# Revit family: MECON mag-flux T4_remote flange
name_source: partatom
category: Rohrzubehör
units: mm (PartAtom-declared; Revit-internal decimal feet)

## family parameters
Arbeitsebenenbasiert = Nein
Beim Laden mit Abzugskörper schneiden = Nein
Bemaßung runder Anschluss = Radius verwenden
Gemeinsam genutzt = Nein
Immer vertikal = Ja
OmniClass-Nummer = 23.60.10.17
OmniClass-Titel = Flow Meters
Teiletyp = Ventil - Zerlegung in

## types (14) — shared parameters
Approval = VdS
Black = Metal - black
Dark Grey = Metal - RAL7024
Delivery Time = app. 3 weeks
Download Test Certificate = https://download.mecon.de
Glass = Glass-
Grey = Metal - grey
Hersteller = MECON GmbH, Röntgenstraße 105, 50169 Kerpen, Germany
IfcExportAs = IfcFlowMeter
IfcExportType = FLOWMETER
Operating Manual = https://www.mecon.de
URL = https://www.mecon.de
VdS Approval = https://www.mecon.de
Website Product = https://www.mecon.de
iFM = Nein
iLPCB = Nein
iVdS = Ja
zero-valued in all types: Vorgabe-Ansicht

## per-type parameters (varying)
| type | Build in Length | Flow Range | Modell | Nominal_Diameter | Nominal_Radius | Order Code | iB | iD1 | iD2 | iH | iR1 |
| DN 300 / PN 16, 0-42411 l/min, 0-11200 USgpm | 500 mm | 0 - 42411 l/min / 0 - 11200 USgpm | Flange connection DN 300 PN 16, lining: hard rubber, electrodes: stainless steel, remote, 230 V AC, 50/60 Hz, 4 - 20 mA, with connector for transducer | 300 mm | 150 mm | T4-H-D300-1-21BB4L | 200 mm  [stored 0.656168 ft] | 520 mm | 310 mm | 213 mm  [stored 0.698819 ft] | 154 mm  [stored 0.505249 ft] |
| DN 250 / PN 16, 0-29500 l/min, 0-7800 USgpm | 450 mm | 0 - 29500 l/min / 0 - 7800 USgpm | Flange connection DN 250 PN 16, lining: hard rubber, electrodes: stainless steel, remote, 230 V AC, 50/60 Hz, 4 - 20 mA, with connector for transducer | 250 mm | 125 mm | T4-H-D250-1-21BB4L | 200 mm  [stored 0.656168 ft] | 440 mm | 270 mm | 180 mm  [stored 0.590551 ft] | 129 mm  [stored 0.423228 ft] |
| DN 200 / PN 16, 0-18850 l/min, 0-5000 USgpm | 350 mm | 0 - 18850 l/min / 0 - 5000 USgpm | Flange connection DN 200 PN 16, lining: hard rubber, electrodes: stainless steel, remote, 230 V AC, 50/60 Hz, 4 - 20 mA, with connector for transducer | 200 mm | 100 mm | T4-H-D200-1-21BB4L | 200 mm  [stored 0.656168 ft] | 350 mm | 225 mm  [stored 0.738189 ft] | 143 mm | 104 mm |
| DN 150 / PN 16, 0-10600 l/min, 0-2800 USgpm | 300 mm | 0 - 10600 l/min / 0 - 2800 USgpm | Flange connection DN 150 PN 16, lining: hard rubber, electrodes: stainless steel, remote, 230 V AC, 50/60 Hz, 4 - 20 mA, with connector for transducer | 150 mm | 75 mm | T4-H-D150-1-21BB4L | 120 mm  [stored 0.393701 ft] | 285 mm | 192.5 mm  [stored 0.631562 ft] | 117 mm  [stored 0.383858 ft] | 79 mm |
| DN 125 / PN 16, 0-7350 l/min, 0-1950 USgpm | 250 mm | 0 - 7350 l/min / 0 - 1950 USgpm | Flange connection DN 125 PN 16, lining: hard rubber, electrodes: stainless steel, remote, 230 V AC, 50/60 Hz, 4 - 20 mA, with connector for transducer | 125 mm | 63 mm | T4-H-D125-1-21BB4L | 120 mm  [stored 0.393701 ft] | 240 mm  [stored 0.787402 ft] | 170 mm  [stored 0.557743 ft] | 98 mm  [stored 0.321522 ft] | 66.5 mm |
| DN 100 / PN 16, 0-4700 l/min, 0-1250 USgpm | 250 mm | 0 - 4700 l/min / 0 - 1250 USgpm | Flange connection DN 100 PN 16, lining: hard rubber, electrodes: stainless steel, remote, 230 V AC, 50/60 Hz, 4 - 20 mA, with connector for transducer | 100 mm | 50 mm | T4-H-D100-1-21BB4L | 120 mm  [stored 0.393701 ft] | 210 mm  [stored 0.688976 ft] | 155 mm  [stored 0.50853 ft] | 86 mm  [stored 0.282152 ft] | 54 mm |
| DN 80 / PN 16, 0-3000 l/min, 0-800 USgpm | 200 mm  [stored 0.656168 ft] | 0 - 3000 l/min / 0 - 800 USgpm | Flange connection DN 80 PN 16, lining: hard rubber, electrodes: stainless steel, remote, 230 V AC, 50/60 Hz, 4 - 20 mA, with connector for transducer | 80 mm | 40 mm | T4-H-D080-1-21BB4L | 80 mm  [stored 0.262467 ft] | 170 mm  [stored 0.557743 ft] | 135 mm  [stored 0.442913 ft] | 70 mm  [stored 0.229659 ft] | 44 mm  [stored 0.144357 ft] |
| DN 65 / PN 16, 0-2000 l/min, 0-525 USgpm | 200 mm  [stored 0.656168 ft] | 0 - 2000 l/min / 0 - 525 USgpm | Flange connection DN 65 PN 16, lining: hard rubber, electrodes: stainless steel, remote, 230 V AC, 50/60 Hz, 4 - 20 mA, with connector for transducer | 65 mm | 33 mm | T4-H-D065-1-21BB4L | 80 mm  [stored 0.262467 ft] | 155 mm  [stored 0.50853 ft] | 127.5 mm  [stored 0.418307 ft] | 63 mm  [stored 0.206693 ft] | 36.5 mm  [stored 0.119751 ft] |
| DN 50 / PN 40, 0-1180 l/min, 0-310 USgpm | 200 mm  [stored 0.656168 ft] | 0 - 1180 l/min / 0 - 310 USgpm | Flange connection DN 50 PN 40, lining: hard rubber, electrodes: stainless steel, remote, 230 V AC, 50/60 Hz, 4 - 20 mA, with connector for transducer | 50 mm | 25 mm | T4-H-D050-1-21BB4L | 80 mm  [stored 0.262467 ft] | 140 mm  [stored 0.459318 ft] | 120 mm  [stored 0.393701 ft] | 57 mm  [stored 0.187008 ft] | 29 mm  [stored 0.0951444 ft] |
| DN 40 / PN 40, 0-750 l/min, 0-200 USgpm | 200 mm  [stored 0.656168 ft] | 0 - 750 l/min / 0 - 200 USgpm | Flange connection DN 40 PN 40, lining: hard rubber, electrodes: stainless steel, remote, 230 V AC, 50/60 Hz, 4 - 20 mA, with connector for transducer | 40 mm | 20 mm | T4-H-D040-1-21BB4L | 80 mm  [stored 0.262467 ft] | 130 mm  [stored 0.426509 ft] | 115 mm  [stored 0.377297 ft] | 53 mm  [stored 0.173885 ft] | 24 mm  [stored 0.0787402 ft] |
| DN 32 / PN 40, 0-480 l/min, 0-128 USgpm | 200 mm  [stored 0.656168 ft] | 0 - 480 l/min / 0 - 128 USgpm | Flange connection DN 32 PN 40, lining: hard rubber, electrodes: stainless steel, remote, 230 V AC, 50/60 Hz, 4 - 20 mA, with connector for transducer | 32 mm | 16 mm | T4-H-D032-1-21BB4L | 80 mm  [stored 0.262467 ft] | 130 mm  [stored 0.426509 ft] | 115 mm  [stored 0.377297 ft] | 53 mm  [stored 0.173885 ft] | 20 mm  [stored 0.0656168 ft] |
| DN 25 / PN 40, 0-295 l/min, 0-78 USgpm | 200 mm  [stored 0.656168 ft] | 0 - 295 l/min / 0 - 78 USgpm | Flange connection DN 25 PN 40, lining: hard rubber, electrodes: stainless steel, remote, 230 V AC, 50/60 Hz, 4 - 20 mA, with connector for transducer | 25 mm | 13 mm | T4-H-D025-1-21BB4L | 80 mm  [stored 0.262467 ft] | 130 mm  [stored 0.426509 ft] | 115 mm  [stored 0.377297 ft] | 53 mm  [stored 0.173885 ft] | 16.5 mm  [stored 0.0541339 ft] |
| DN 20 / PN 40, 0-188 l/min, 0-50 USgpm | 200 mm  [stored 0.656168 ft] | 0 - 188 l/min / 0 - 50 USgpm | Flange connection DN 20 PN 40, lining: hard rubber, electrodes: stainless steel, remote, 230 V AC, 50/60 Hz, 4 - 20 mA, with connector for transducer | 20 mm | 10 mm | T4-H-D020-1-21BB4L | 80 mm  [stored 0.262467 ft] | 130 mm  [stored 0.426509 ft] | 115 mm  [stored 0.377297 ft] | 53 mm  [stored 0.173885 ft] | 14 mm  [stored 0.0459318 ft] |
| DN 15 / PN 40, 0-106 l/min, 0-28 USgpm | 200 mm  [stored 0.656168 ft] | 0 - 106 l/min / 0 - 28 USgpm | Flange connection: DN 15 PN 40, lining: hard rubber, electrodes: stainless steel, remote, 230 V AC, 50/60 Hz, 4 - 20 mA, with connector for transducer | 15 mm | 8 mm | T4-H-D015-1-21BB4L | 80 mm  [stored 0.262467 ft] | 130 mm  [stored 0.426509 ft] | 115 mm  [stored 0.377297 ft] | 52 mm | 11.5 mm  [stored 0.0377297 ft] |

note: column(s) folded — value = type name in every type: Typenkommentare

note: [stored X ft] marks values corroborated as IEEE doubles in the binary element streams (Revit-internal decimal feet)
